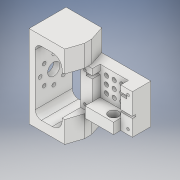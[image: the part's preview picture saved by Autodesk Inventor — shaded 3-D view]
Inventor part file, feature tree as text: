
AUTODESK INVENTOR PART (.ipt)
format: ipt  version: 2018 (Build 220112000, 112)  size: 369,664 bytes
history: native  units: in
note: dims shown in document units (in); Inventor stores cm internally (conversion verified against a paired STEP export)
features: extrude x13, sketch x13, chamfer x4, fillet x3, pattern_linear x1, plane x1
ambient origin geometry x8: Origin, YZ Plane, XZ Plane, XY Plane, X Axis, Y Axis, Z Axis, Center Point
bodies: Solid1 (feature_tree)
feature tree (35):
  extrude  "Servo_Housing"  Depth=1.2598in
  extrude  "Servo_Opening"  Depth=0.1969in
  extrude  "Cable_Opening"  Depth=0.9055in
  extrude  "Cover_Mounting_Holes"  Depth=0.0906in
  extrude  "Pin"  Depth=0.2461in TaperAngle=0.0deg
  extrude  "Shaft_Opening"  Depth=1.6535in
  extrude  "Nut_Slot"  Depth=0.9055in
  extrude  "Connection_Adapter"  Depth=0.1969in
  extrude  "Docking_Holes_Front"  Depth=0.1969in
  extrude  "Cable_Opening_Front"  Depth=0.0866in
  extrude  "Insert_Opening"  Depth=1.6535in
  fillet  "Fillet4"  Radius=1.6535in
  chamfer  "Chamfer1"  Distance=0.6299in
  chamfer  "Chamfer2"  Distance=1.378in
  chamfer  "Chamfer3"  Distance=0.689in
  chamfer  "Chamfer4"  Distance=0.9449in
  fillet  "Fillet5"  Radius=0.4724in
  extrude  "Heat_dissipation_Hole"  Depth=0.1772in TaperAngle=0.0deg
  pattern_linear  "Rectangular Pattern1"  Spacing1=0.2283in  [1 undecoded]
  extrude  "Extrusion22"  Depth=0.1772in
  fillet  "Fillet6"  Radius=0.1969in
  plane  "Work Plane1"
  sketch  "Sketch2"  dims[d0=1.6535in d1=1.2598in]
  sketch  "Sketch4"  dims[d2=0.5906in d3=0.0in d6=0.1969in]
  sketch  "Sketch5"  dims[d7=0.6299in d8=0.9055in]
  sketch  "Sketch6"  dims[d11=0.3425in d14=0.0906in]
  sketch  "Sketch10"  dims[d15=0.0906in d16=0.2461in d17=0.0in]
  sketch  "Sketch11"  dims[d20=0.0984in d21=0.0in d22=1.6535in]
  sketch  "Sketch12"  dims[d23=0.8268in d24=0.9055in]
  sketch  "Sketch15"  dims[d25=0.4528in d26=0.1969in]
  sketch  "Sketch17"  dims[d27=0.1969in d28=0.1969in]
  sketch  "Sketch19"  dims[d29=0.0866in d30=0.0866in]
  sketch  "Sketch22"  dims[d31=0.0866in d32=0.0866in d33=1.6535in]
  sketch  "Sketch24"  dims[d34=0.8268in]
  sketch  "Sketch25"  dims[d35=1.2598in d36=0.6299in d37=1.378in d38=0.689in d39=0.9449in d40=0.4724in d41=0.0787in d42=0.0in d63=0.2283in d64=0.0in d65=0.126in d67=0.1969in d68=0.0in d69=0.6024in d70=0.126in d73=0.315in d74=0.2244in d75=0.0in d99=1.1811in d100=0.0in d111=0.3937in d113=0.2362in d114=0.689in d116=0.3937in d117=0.8583in d118=0.2362in d119=0.689in d120=1.2913in d121=0.8661in d122=2.0472in d123=1.0236in d124=1.1811in d125=0.5906in d126=0.1181in d127=0.1181in d128=0.1181in d129=0.1181in d130=0.1181in d131=0.1181in d132=0.1181in d133=0.1181in d134=45.0deg d135=45.0deg d136=0.3937in d137=0.0in d140=0.3937in d141=2.0472in d142=1.0236in d143=1.1811in d144=0.5906in d145=0.3937in d146=0.0in d159=0.1969in d160=0.0in d161=0.2953in d166=0.126in d167=0.126in d168=0.126in d169=0.126in d171=0.0591in d173=0.315in d175=1.2913in d176=0.0945in d177=0.0748in d178=0.4724in d179=0.0787in d180=0.1237in d181=0.4724in d182=0.0787in d183=0.1237in d184=0.4724in d185=0.0787in d186=0.1237in d187=0.4724in d188=0.0787in d189=0.1237in d190=0.1969in d191=0.1969in d192=0.1378in d193=0.2126in d194=0.2067in d195=0.3937in d196=0.0in d197=1.1811in d199=0.2461in d200=0.9055in d201=1.1811in d203=0.2461in d204=0.3465in d205=0.5906in d206=0.2953in d207=0.3937in d208=0.3937in d209=0.0in d210=0.0787in d211=0.1772in]
note: 1 required parameter value undecoded (feature->parameter linkage not recoverable at this tier; creation-order binding heuristic only, values carry confidence <= 0.55)
